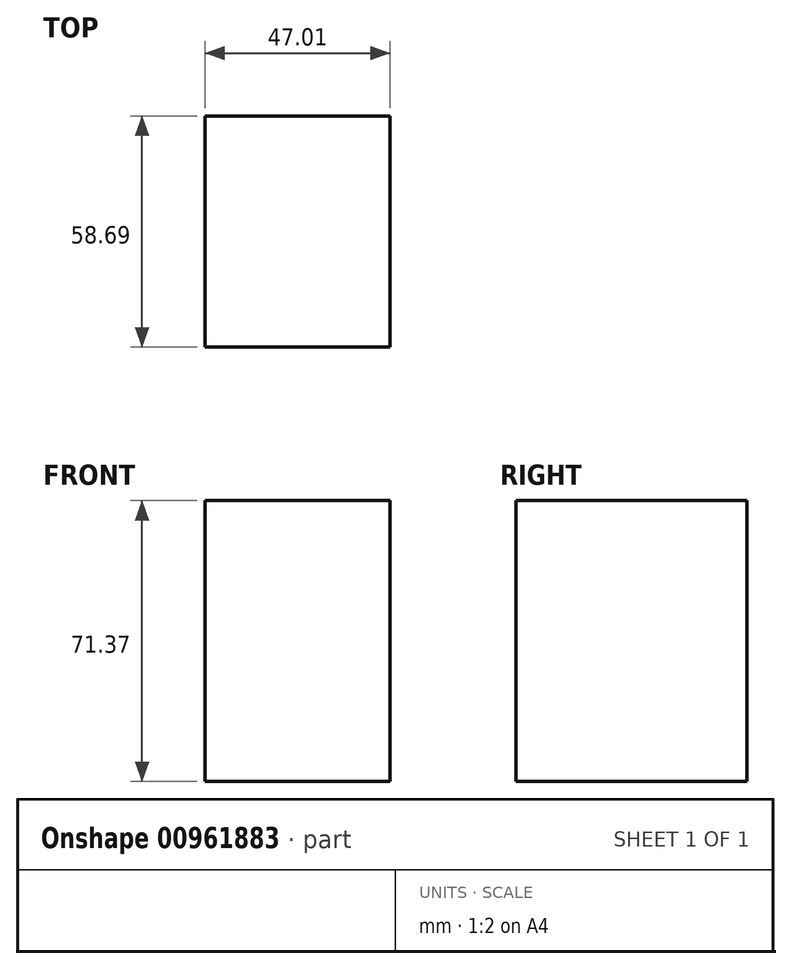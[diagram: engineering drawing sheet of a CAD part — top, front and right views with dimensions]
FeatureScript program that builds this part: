
annotation { "Feature Type Name" : "Feature", "Feature Type Description" : "" }
export const myFeature = defineFeature(function(context is Context, id is Id, definition is map)
    precondition{}
    {
        {
            var Q0;
            Q0=qCreatedBy(makeId("Top.planeOp"),FACE);
            var sketch = newSketch(context, id + "F0", { "sketchPlane" : qUnion([Q0])});
            skLineSegment(sketch, "E0.bottom", {"start": v(0, 0) * mm, "end": v(-13.58, 0) * mm});
            skLineSegment(sketch, "E0.top", {"start": v(0, -36.94) * mm, "end": v(-13.58, -36.94) * mm});
            skLineSegment(sketch, "E0.left", {"start": v(0, 0) * mm, "end": v(0, -36.94) * mm});
            skLineSegment(sketch, "E0.right", {"start": v(-13.58, 0) * mm, "end": v(-13.58, -36.94) * mm});
            skLineSegment(sketch, "E1.bottom", {"start": v(0, -36.94) * mm, "end": v(33.43, -36.94) * mm});
            skLineSegment(sketch, "E1.top", {"start": v(0, 0) * mm, "end": v(33.43, 0) * mm});
            skLineSegment(sketch, "E1.left", {"start": v(0, -36.94) * mm, "end": v(0, 0) * mm});
            skLineSegment(sketch, "E1.right", {"start": v(33.43, -36.94) * mm, "end": v(33.43, 0) * mm});
            skLineSegment(sketch, "E2.bottom", {"start": v(-13.58, 0) * mm, "end": v(33.43, 0) * mm});
            skLineSegment(sketch, "E2.top", {"start": v(-13.58, 21.75) * mm, "end": v(33.43, 21.75) * mm});
            skLineSegment(sketch, "E2.left", {"start": v(-13.58, 0) * mm, "end": v(-13.58, 21.75) * mm});
            skLineSegment(sketch, "E2.right", {"start": v(33.43, 0) * mm, "end": v(33.43, 21.75) * mm});
            skSolve(sketch);
        }
        {
            var Q0;
            Q0=makeQuery(id+"F0.imprint","IMPRINT",FACE,{"disambiguationData":[TD([[makeQuery(id+"F0.imprint","IMPRINT",EDGE,{"derivedFrom":sQuery(id+"F0.wireOp",EDGE,"E1.bottom")}),1.0]])]});
            var Q1;
            Q1=makeQuery(id+"F0.imprint","IMPRINT",FACE,{"disambiguationData":[TD([[makeQuery(id+"F0.imprint","IMPRINT",EDGE,{"derivedFrom":sQuery(id+"F0.wireOp",EDGE,"E0.top")}),-1.0]])]});
            var Q2;
            Q2=makeQuery(id+"F0.imprint","IMPRINT",FACE,{"disambiguationData":[TD([[makeQuery(id+"F0.imprint","IMPRINT",EDGE,{"derivedFrom":sQuery(id+"F0.wireOp",EDGE,"E2.top")}),-1.0]])]});
            extrude(context, id + "F1", {"entities" : qUnion([Q0, Q1, Q2]), "depth" : 71.37 * mm, "offsetDistance" : 25.4 * mm});
        }
    });
